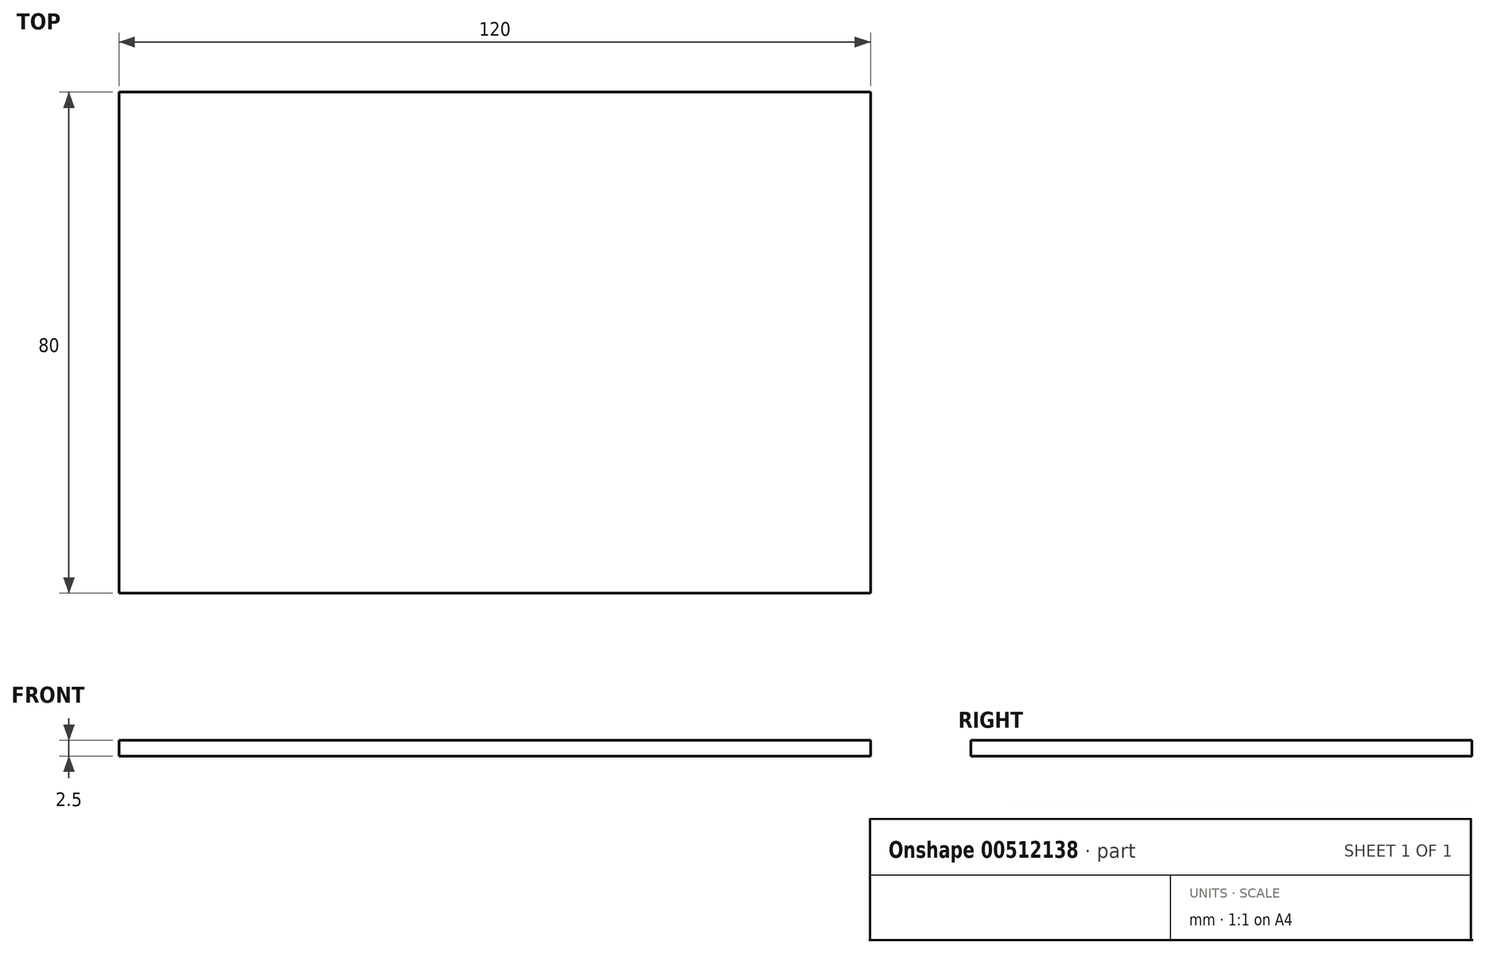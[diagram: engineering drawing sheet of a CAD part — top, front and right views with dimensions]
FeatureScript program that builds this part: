
annotation { "Feature Type Name" : "Feature", "Feature Type Description" : "" }
export const myFeature = defineFeature(function(context is Context, id is Id, definition is map)
    precondition{}
    {
        {
            var Q0;
            Q0=qCreatedBy(makeId("Top.planeOp"),FACE);
            var sketch = newSketch(context, id + "F0", { "sketchPlane" : qUnion([Q0])});
            skLineSegment(sketch, "E0.left", {"start": v(60, 40) * mm, "end": v(60, -40) * mm});
            skLineSegment(sketch, "E0.right", {"start": v(-60, 40) * mm, "end": v(-60, -40) * mm});
            skPoint(sketch, "E0.middle", {"position": v(0, 0) * mm});
            skLineSegment(sketch, "E1", {"start": v(-60, 40) * mm, "end": v(60, 40) * mm});
            skLineSegment(sketch, "E2", {"start": v(-60, -40) * mm, "end": v(60, -40) * mm});
            skSolve(sketch);
        }
        {
            var Q0;
            {var subQ5=sQuery(id+"F0.wireOp",EDGE,"E0.left");Q0=makeQuery(id+"F0.imprint","IMPRINT",FACE,{"disambiguationData":[TD([[makeQuery(id+"F0.imprint","IMPRINT",EDGE,{"derivedFrom":subQ5}),-1.0]])]});}
            extrude(context, id + "F1", {"entities" : qUnion([Q0]), "depth" : 2.5 * mm, "offsetDistance" : 25 * mm});
        }
    });
